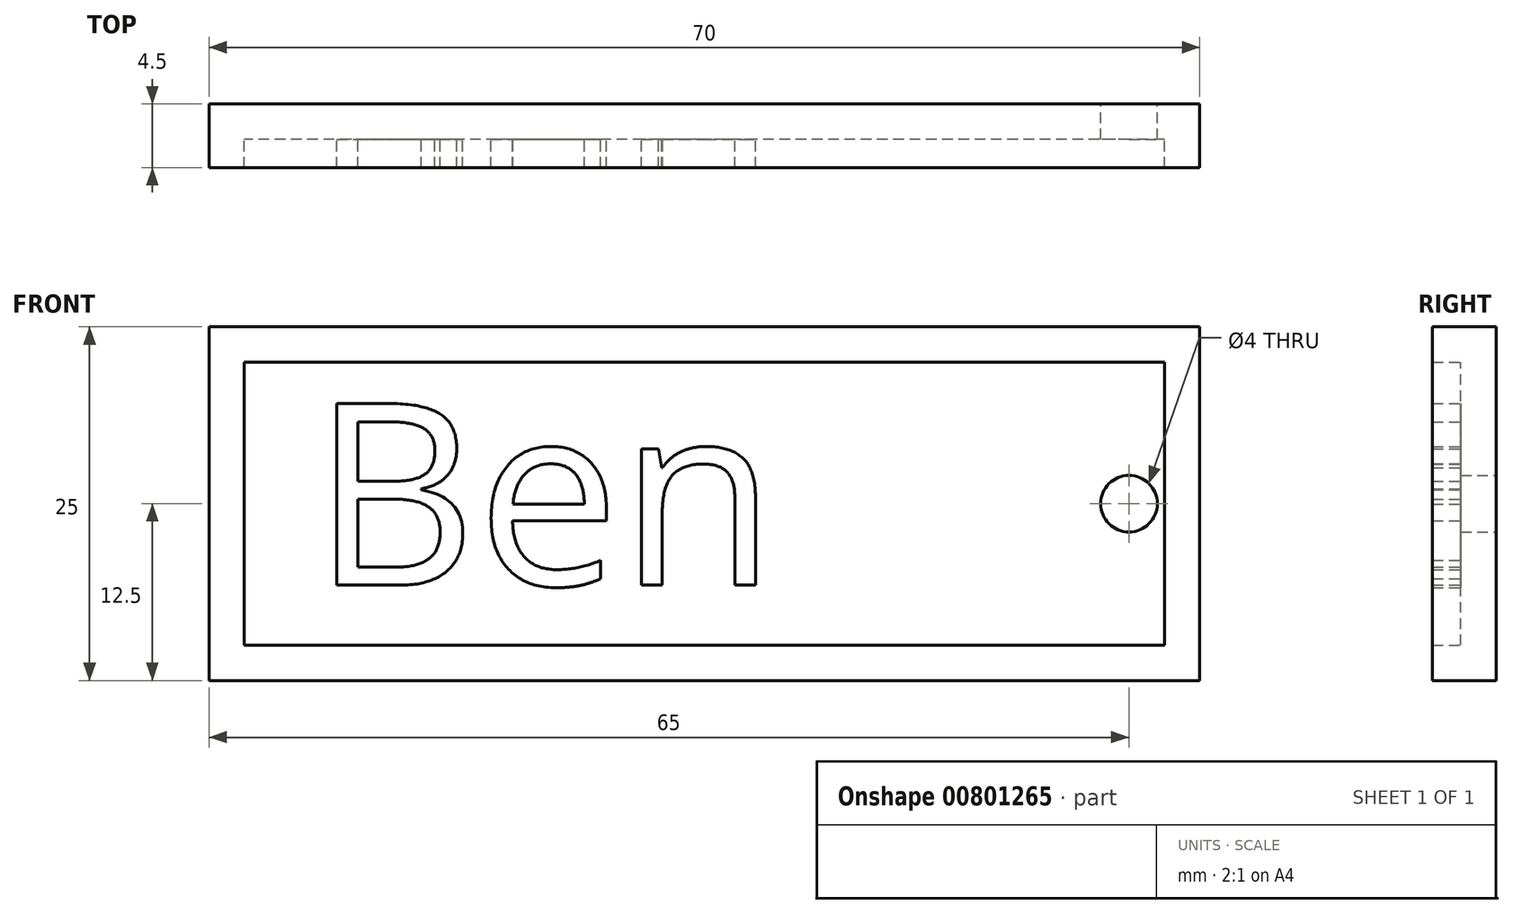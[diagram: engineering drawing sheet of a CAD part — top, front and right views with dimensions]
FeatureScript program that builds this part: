
annotation { "Feature Type Name" : "Feature", "Feature Type Description" : "" }
export const myFeature = defineFeature(function(context is Context, id is Id, definition is map)
    precondition{}
    {
        {
            var Q0;
            Q0=qCreatedBy(makeId("Front.planeOp"),FACE);
            var sketch = newSketch(context, id + "F0", { "sketchPlane" : qUnion([Q0])});
            skLineSegment(sketch, "E0.bottom", {"start": v(0, 0) * mm, "end": v(70, 0) * mm});
            skLineSegment(sketch, "E0.top", {"start": v(0, 25) * mm, "end": v(70, 25) * mm});
            skLineSegment(sketch, "E0.left", {"start": v(0, 0) * mm, "end": v(0, 25) * mm});
            skLineSegment(sketch, "E0.right", {"start": v(70, 0) * mm, "end": v(70, 25) * mm});
            skSolve(sketch);
        }
        {
            var Q0;
            Q0=makeQuery(id+"F0.imprint","IMPRINT",FACE,{"disambiguationData":[TD([[makeQuery(id+"F0.imprint","IMPRINT",EDGE,{"derivedFrom":sQuery(id+"F0.wireOp",EDGE,"E0.bottom")}),1.0]])]});
            extrude(context, id + "F1", {"entities" : qUnion([Q0]), "depth" : 2.5 * mm, "offsetDistance" : 25 * mm});
        }
        {
            var Q0;
            Q0=makeQuery(id+"F1.opExtrude","CAP_FACE",FACE,{"disambiguationData":[OSD([sQuery(id+"F0.wireOp",EDGE,"E0.bottom"),sQuery(id+"F0.wireOp",EDGE,"E0.top"),sQuery(id+"F0.wireOp",EDGE,"E0.left"),sQuery(id+"F0.wireOp",EDGE,"E0.right")])],"isStart":false});
            var sketch = newSketch(context, id + "F2", { "sketchPlane" : qUnion([Q0])});
            skLineSegment(sketch, "E1.0", {"start": v(67.5, 22.5) * mm, "end": v(2.5, 22.5) * mm});
            skLineSegment(sketch, "E1.1", {"start": v(67.5, 2.5) * mm, "end": v(67.5, 22.5) * mm});
            skLineSegment(sketch, "E1.2", {"start": v(2.5, 2.5) * mm, "end": v(67.5, 2.5) * mm});
            skLineSegment(sketch, "E1.3", {"start": v(2.5, 22.5) * mm, "end": v(2.5, 2.5) * mm});
            skSolve(sketch);
        }
        {
            var Q0;
            Q0=makeQuery(id+"F2.imprint","IMPRINT",FACE,{"disambiguationData":[TD([[makeQuery(id+"F2.imprint","IMPRINT",EDGE,{"derivedFrom":sQuery(id+"F2.wireOp",EDGE,"E1.0")}),-1.0]])]});
            extrude(context, id + "F3", {"entities" : qUnion([Q0]), "operationType" : NewBodyOperationType.ADD, "depth" : 2 * mm, "offsetDistance" : 25 * mm});
        }
        {
            var Q0;
            Q0=makeQuery(id+"F1.opExtrude","CAP_FACE",FACE,{"disambiguationData":[OSD([sQuery(id+"F0.wireOp",EDGE,"E0.bottom"),sQuery(id+"F0.wireOp",EDGE,"E0.top"),sQuery(id+"F0.wireOp",EDGE,"E0.left"),sQuery(id+"F0.wireOp",EDGE,"E0.right")])],"isStart":false});
            var sketch = newSketch(context, id + "F4", { "sketchPlane" : qUnion([Q0])});
            skText(sketch, "E2", { "text": "Ben", "fontName": "OpenSans-Regular.ttf"});
            const initialGuessF4  = {"E2": [0.00727, 0.00674, 1, 0, 0.01295]};
            skSetInitialGuess(sketch, initialGuessF4);
            skSolve(sketch);
        }
        {
            var Q0;
            Q0 = qSketchRegion(id + "F4", true);
            extrude(context, id + "F5", {"entities" : qUnion([Q0]), "operationType" : NewBodyOperationType.ADD, "depth" : 2 * mm, "offsetDistance" : 25 * mm});
        }
        {
            var Q0;
            Q0=makeQuery(id+"F1.opExtrude","CAP_FACE",FACE,{"disambiguationData":[OSD([sQuery(id+"F0.wireOp",EDGE,"E0.bottom"),sQuery(id+"F0.wireOp",EDGE,"E0.top"),sQuery(id+"F0.wireOp",EDGE,"E0.left"),sQuery(id+"F0.wireOp",EDGE,"E0.right")])],"isStart":true});
            var sketch = newSketch(context, id + "F6", { "sketchPlane" : qUnion([Q0])});
            skCircle(sketch, "E3", {"center": v(-65, 12.5) * mm, "radius": 1.75 * mm});
            skPoint(sketch, "E3.centerSnap0", {"position": v(-70, 12.5) * mm});
            skSolve(sketch);
        }
        {
            var Q0;
            Q0=sQuery(id+"F6.wireOp",VERTEX,"E3.center");
            var Q1;
            Q1=makeQuery(id+"F1.opExtrude","SWEPT_BODY",BODY,{"disambiguationData":[OSD([sQuery(id+"F0.wireOp",EDGE,"E0.bottom"),sQuery(id+"F0.wireOp",EDGE,"E0.top"),sQuery(id+"F0.wireOp",EDGE,"E0.left"),sQuery(id+"F0.wireOp",EDGE,"E0.right")])]});
            hole(context, id + "F7", {"style" : HoleStyle.SIMPLE, "endStyle" : HoleEndStyle.THROUGH, "holeDiameter" : 4 * mm, "majorDiameter" : 5 * mm, "isTappedThrough" : true, "tappedDepth" : 12 * mm, "tapClearance" : 3, "locations" : qUnion([Q0]), "scope" : qUnion([Q1])});
        }
    });
